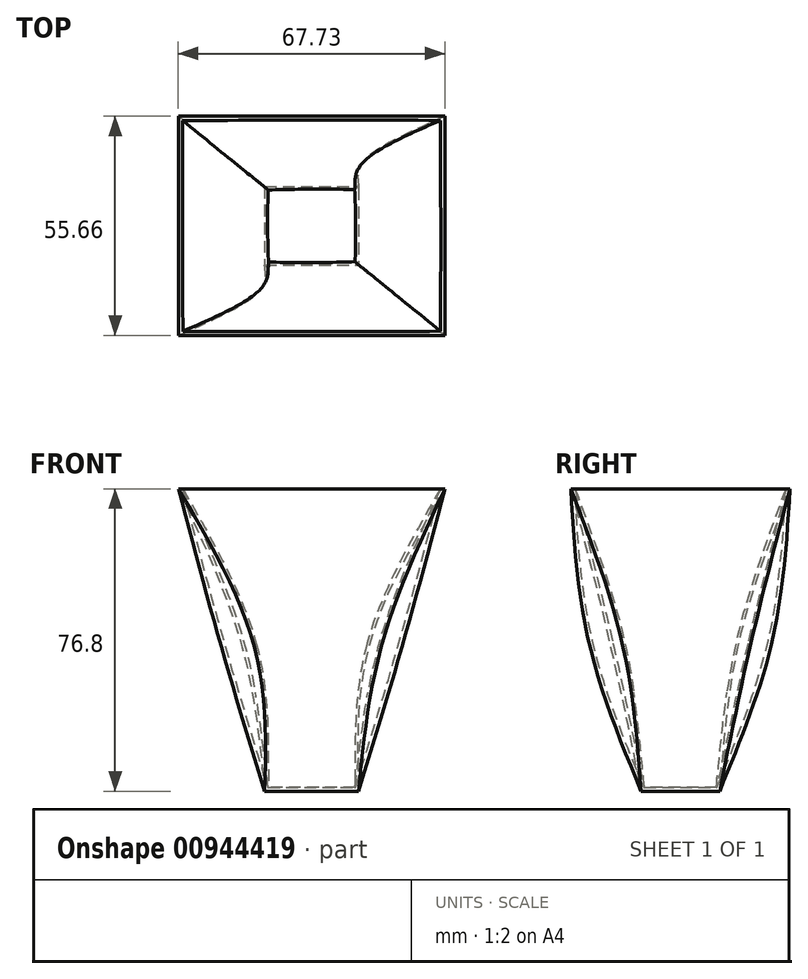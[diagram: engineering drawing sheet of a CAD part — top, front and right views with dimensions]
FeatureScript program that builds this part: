
annotation { "Feature Type Name" : "Feature", "Feature Type Description" : "" }
export const myFeature = defineFeature(function(context is Context, id is Id, definition is map)
    precondition{}
    {
        {
            var Q0;
            Q0=qCreatedBy(makeId("Top.planeOp"),FACE);
            var sketch = newSketch(context, id + "F0", { "sketchPlane" : qUnion([Q0])});
            skLineSegment(sketch, "E0.bottom", {"start": v(-11.91, 10) * mm, "end": v(11.91, 10) * mm});
            skLineSegment(sketch, "E0.top", {"start": v(-11.91, -10) * mm, "end": v(11.91, -10) * mm});
            skLineSegment(sketch, "E0.left", {"start": v(-11.91, 10) * mm, "end": v(-11.91, -10) * mm});
            skLineSegment(sketch, "E0.right", {"start": v(11.91, 10) * mm, "end": v(11.91, -10) * mm});
            skPoint(sketch, "E0.middle", {"position": v(0, 0) * mm});
            skSolve(sketch);
        }
        {
            var Q0;
            Q0=qCreatedBy(makeId("Top.planeOp"),FACE);
            cPlane(context, id + "F1", {"entities" : qUnion([Q0]), "cplaneType" : CPlaneType.OFFSET, "offset" : 37.2 * mm, "width" : 150 * mm, "height" : 150 * mm});
        }
        {
            var Q0;
            Q0=qCreatedBy(id+"F1.planeOp",FACE);
            var sketch = newSketch(context, id + "F2", { "sketchPlane" : qUnion([Q0])});
            skCircle(sketch, "E1", {"center": v(0, 0) * mm, "radius": 23.1 * mm});
            skSolve(sketch);
        }
        {
            var Q0;
            Q0=qCreatedBy(makeId("Top.planeOp"),FACE);
            cPlane(context, id + "F3", {"entities" : qUnion([Q0]), "cplaneType" : CPlaneType.OFFSET, "offset" : 76.8 * mm, "width" : 150 * mm, "height" : 150 * mm});
        }
        {
            var Q0;
            Q0=qCreatedBy(id+"F3.planeOp",FACE);
            var sketch = newSketch(context, id + "F4", { "sketchPlane" : qUnion([Q0])});
            skLineSegment(sketch, "E2.bottom", {"start": v(-33.85, 27.83) * mm, "end": v(33.85, 27.83) * mm});
            skLineSegment(sketch, "E2.top", {"start": v(-33.85, -27.83) * mm, "end": v(33.85, -27.83) * mm});
            skLineSegment(sketch, "E2.left", {"start": v(-33.85, 27.83) * mm, "end": v(-33.85, -27.83) * mm});
            skLineSegment(sketch, "E2.right", {"start": v(33.85, 27.83) * mm, "end": v(33.85, -27.83) * mm});
            skPoint(sketch, "E2.middle", {"position": v(0, 0) * mm});
            skSolve(sketch);
        }
        {
            var Q0;
            Q0=makeQuery(id+"F4.imprint","IMPRINT",FACE,{"disambiguationData":[TD([[makeQuery(id+"F4.imprint","IMPRINT",EDGE,{"derivedFrom":sQuery(id+"F4.wireOp",EDGE,"E2.bottom")}),-1.0]])]});
            var Q1;
            Q1=makeQuery(id+"F2.imprint","IMPRINT",FACE,{"disambiguationData":[TD([[makeQuery(id+"F2.imprint","IMPRINT",EDGE,{"derivedFrom":sQuery(id+"F2.wireOp",EDGE,"E1")}),1.0]])]});
            var Q2;
            Q2=makeQuery(id+"F0.imprint","IMPRINT",FACE,{"disambiguationData":[TD([[makeQuery(id+"F0.imprint","IMPRINT",EDGE,{"derivedFrom":sQuery(id+"F0.wireOp",EDGE,"E0.bottom")}),-1.0]])]});
            loft(context, id + "F5", {"sheetProfilesArray" : [{ "sheetProfileEntities" : qUnion([Q0]) }, { "sheetProfileEntities" : qUnion([Q1]) }, { "sheetProfileEntities" : qUnion([Q2]) }]});
        }
        {
            var Q0;
            Q0=makeQuery(id+"F5.opLoft","CAP_FACE",FACE,{"disambiguationData":[OSD([makeQuery(id+"F4.imprint","IMPRINT",FACE,{"disambiguationData":[TD([[makeQuery(id+"F4.imprint","IMPRINT",EDGE,{"derivedFrom":sQuery(id+"F4.wireOp",EDGE,"E2.bottom")}),-1.0]])]})])],"isStart":true});
            shell(context, id + "F6", {"entities" : qUnion([Q0]), "thickness" : 1 * mm});
        }
    });
